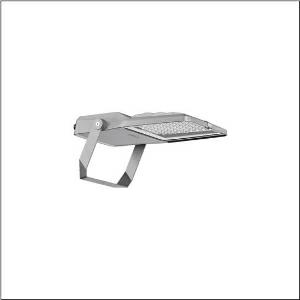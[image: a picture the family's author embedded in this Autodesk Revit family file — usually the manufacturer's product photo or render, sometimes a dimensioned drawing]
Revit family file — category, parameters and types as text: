
# Revit family: floodlight_fl_21_iq_mini___pl61_5xa7771c4c1a_e46d
name_source: partatom
category: Lighting Fixtures
units: mm (PartAtom-declared; Revit-internal decimal feet)

## family parameters
Cut with Voids When Loaded = No
Host = Face
Light Source = No
Part Type = Normal
Room Calculation Point = No
Round Connector Dimension = Use Diameter
Shared = No

## types (1)
- --- (1 x LED, 12490 lm, 87.2 W, 4000K)
    Apparent Load = 87 VA
    CIE Flux Codes = 33 65 98 100 100
    Color Rendering = 70
    Color Temperature = 4000K
    Default Elevation = 1800 mm
    Description = Floodlight FL 21 iQ mini, floodlight, primary light control with lens, of PMMA, primary optical cover: protective disc, of toughened safety glass, transparent, light distribution: PL61, light emission: direct distribution, installation type: surface-mounted, LED, High Power LED, rated luminous flux: 12.490lm, luminous efficacy: 143lm/W, light colour: 740, colour temperature: 4000K, control gear: iQ Comfort/DALI, control: Auto-Match, Temp-Guard, Lumen-Switch, Night-Set, Smart-Wire, Light-Fading, Desk-Remote (wireless, voltage-free reading and setting of iQ features in the workshop via application-optimized NFC function/RFID function), optimised constant luminous flux control (CLO 2.0), with terminal, 6-pole, mains connection: 220..240V, AC, 50/60Hz, start of lifetime: 87W, end of service life: 92W, reduction: 40W, luminaire housing, of diecast aluminium, powder-coated, Siteco® metallic grey (DB 702S), corrosivity category C5 mid according to DIN EN ISO 12944, suitable for swimming pools, chlorine-resistant, sealing non-destructively replaceable, mounting bracket, of steel, galvanised, powder-coated, Siteco® metallic grey (DB 702S), protection rating (complete): IP66, insulation class (complete): insulation class II (safety insulation), certification: CE, ENEC, VDE, protection symbol: D, impact resistance: IK08, permissible operating ambient temperature: -40..+40°C, permissible operating ambient temperature for outdoor applications: -40..+50°C, standard: DIN EN 12944, LABS conformity tested according to VDMA 24364:2018-05, packaging unit: 1 piece

Light Distribution: PL61
    Height = 70 mm
    Lamp = 1 x LED
    Lamp Light Flux = 12490 lm
    Lamp Power = 87.2 W
    Lamp count = 1
    Length = 485 mm
    Luminous efficacy = 143 lm/W
    Manufacturer = Siteco
    ModVariant = No
    Model = 5XA7771C4C1A
    Number of Poles = 1
    OnlyDefault = Yes
    Power Factor = 1
    Product Name = Floodlight FL 21 iQ mini | PL61
    Product group = floodlight | pylon annexe
    ProductGroupID = 6200
    Protection Class = Protection class II
    Protection Degree = IP 66
    RLX_Detail_Level = 1
    RLX_Emergency_Light_Flux = 0 lm
    RLX_Emergency_Type = 0
    RLX_Emergency_Type_DB = No
    RlxData = <blob elided: 96505 chars, md5=f21ff06f>
    Socket = socket
    Standby Power = 0 W
    System Light Flux = 12490 lm
    System Power = 87 W
    Type Comments = factory setting: luminous flux: 100 % | dim-lin: 254 | 456 mA
    Type Image = l_1006845.jpg
    URL = http://relux.com
    VarID = @adj_173260
    Voltage = 0 V
    Weight = 0.00 kg
    Width = 337 mm

## geometry (parser evidence)
native form markers: Blend x4, Sweep x14
no freeform markers — native parametric forms only
